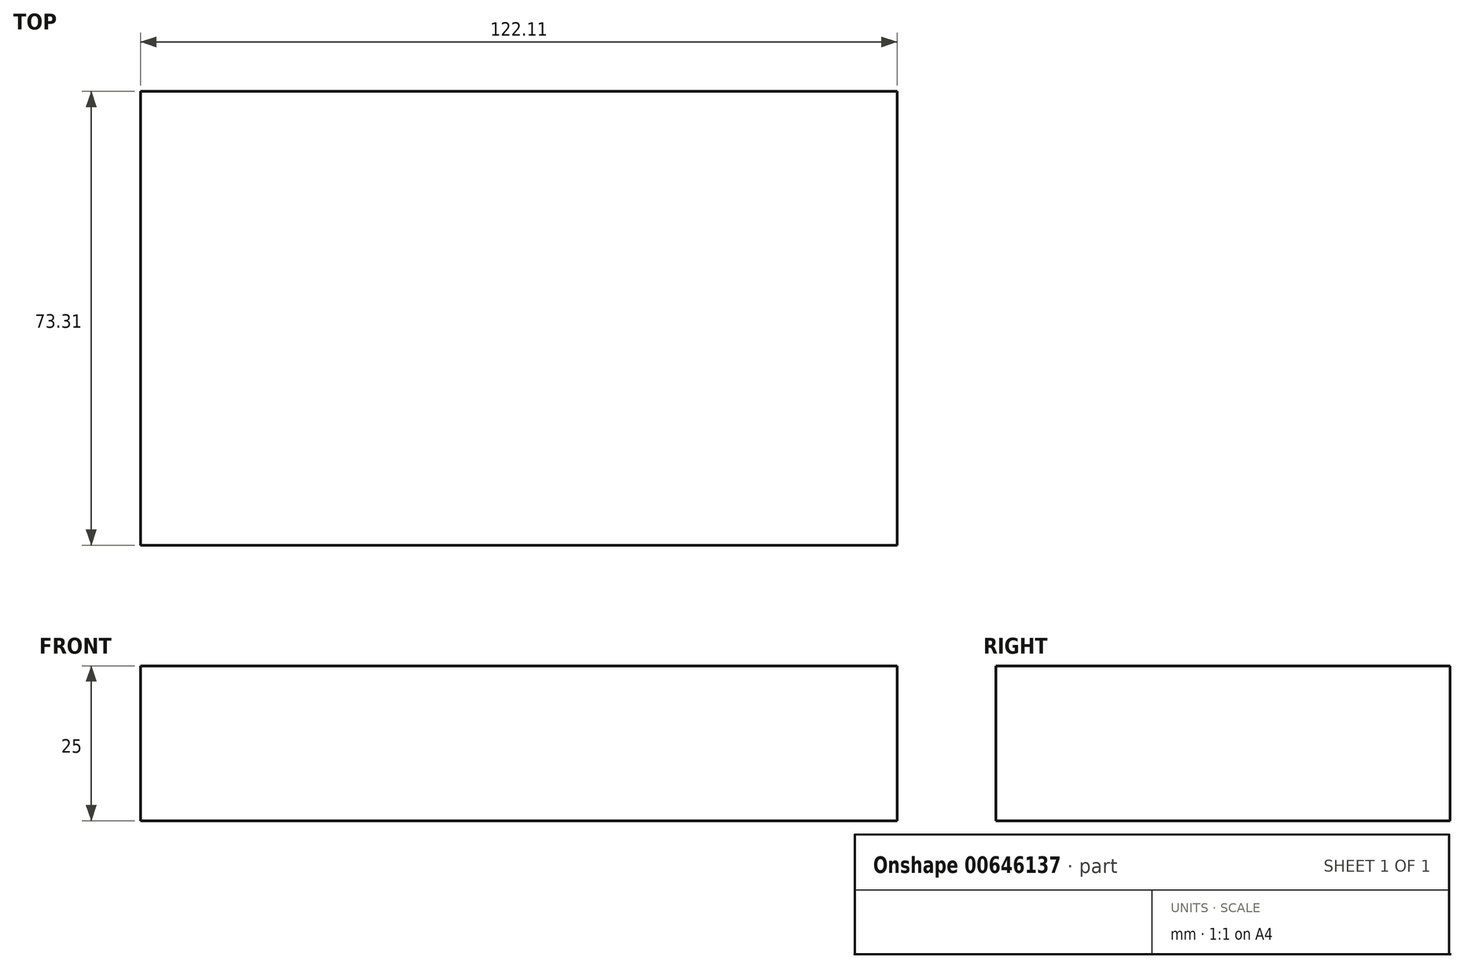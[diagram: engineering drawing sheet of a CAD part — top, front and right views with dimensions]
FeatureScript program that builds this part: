
annotation { "Feature Type Name" : "Feature", "Feature Type Description" : "" }
export const myFeature = defineFeature(function(context is Context, id is Id, definition is map)
    precondition{}
    {
        {
            var Q0;
            Q0=qCreatedBy(makeId("Top.planeOp"),FACE);
            var sketch = newSketch(context, id + "F0", { "sketchPlane" : qUnion([Q0])});
            skLineSegment(sketch, "E0.bottom", {"start": v(-60.33, 36.93) * mm, "end": v(61.78, 36.93) * mm});
            skLineSegment(sketch, "E0.top", {"start": v(-60.33, -36.38) * mm, "end": v(61.78, -36.38) * mm});
            skLineSegment(sketch, "E0.left", {"start": v(-60.33, 36.93) * mm, "end": v(-60.33, -36.38) * mm});
            skLineSegment(sketch, "E0.right", {"start": v(61.78, 36.93) * mm, "end": v(61.78, -36.38) * mm});
            skSolve(sketch);
        }
        {
            var Q0;
            Q0=makeQuery(id+"F0.imprint","IMPRINT",FACE,{"disambiguationData":[TD([[makeQuery(id+"F0.imprint","IMPRINT",EDGE,{"derivedFrom":sQuery(id+"F0.wireOp",EDGE,"E0.bottom")}),-1.0]])]});
            extrude(context, id + "F1", {"entities" : qUnion([Q0]), "depth" : 25 * mm, "offsetDistance" : 25 * mm});
        }
        {
            var Q0;
            Q0=makeQuery(id+"F1.opExtrude","SWEPT_BODY",BODY,{"disambiguationData":[OSD([sQuery(id+"F0.wireOp",EDGE,"E0.bottom"),sQuery(id+"F0.wireOp",EDGE,"E0.top"),sQuery(id+"F0.wireOp",EDGE,"E0.left"),sQuery(id+"F0.wireOp",EDGE,"E0.right")])]});
            transform(context, id + "F2", {"entities" : qUnion([Q0]), "transformType" : TransformType.TRANSLATION_3D, "dx" : 0 * mm, "dy" : 0 * mm, "dz" : -10 * mm, "makeCopy" : false});
        }
    });
